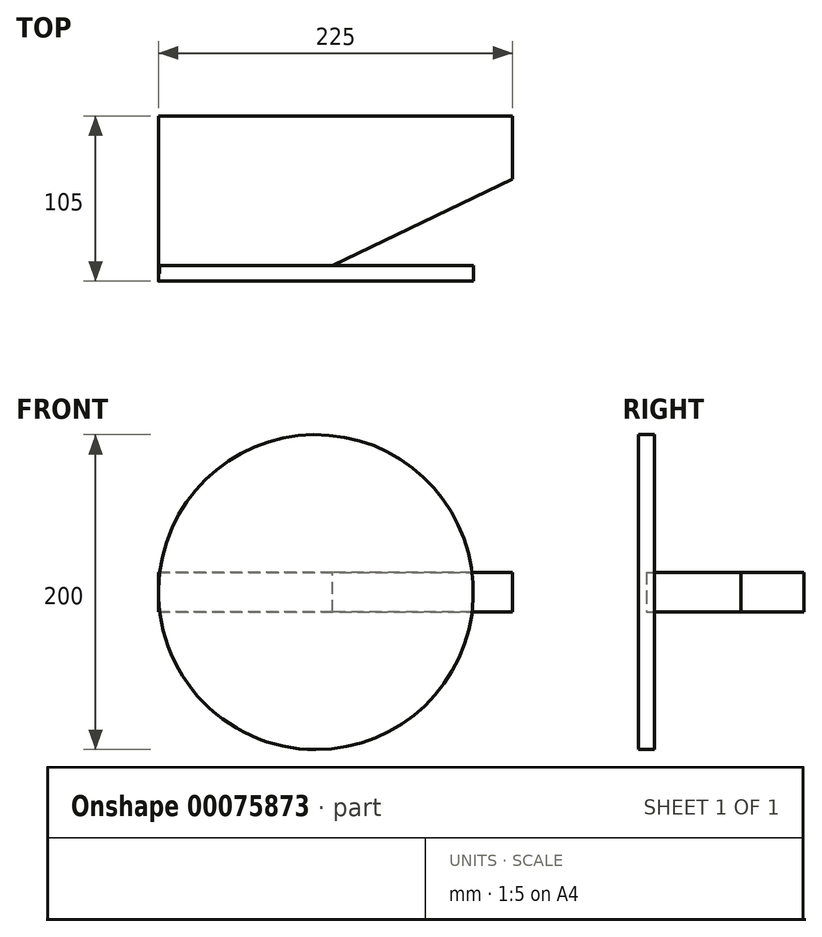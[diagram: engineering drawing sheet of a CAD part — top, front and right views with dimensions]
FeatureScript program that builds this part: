
annotation { "Feature Type Name" : "Feature", "Feature Type Description" : "" }
export const myFeature = defineFeature(function(context is Context, id is Id, definition is map)
    precondition{}
    {
        {
            var Q0;
            Q0=qCreatedBy(makeId("Front.planeOp"),FACE);
            var sketch = newSketch(context, id + "F0", { "sketchPlane" : qUnion([Q0])});
            skCircle(sketch, "E0", {"center": v(0, 0) * mm, "radius": 100 * mm});
            skSolve(sketch);
        }
        {
            var Q0;
            Q0 = qSketchRegion(id + "F0", true);
            extrude(context, id + "F1", {"entities" : qUnion([Q0]), "endBound" : BoundingType.SYMMETRIC, "depth" : 10 * mm});
        }
        {
            var Q0;
            Q0=qCreatedBy(makeId("Top.planeOp"),FACE);
            var sketch = newSketch(context, id + "F2", { "sketchPlane" : qUnion([Q0])});
            skLineSegment(sketch, "E1", {"start": v(0, 0) * mm, "end": v(-100, 0) * mm});
            skLineSegment(sketch, "E2", {"start": v(-100, 0) * mm, "end": v(-100, 100) * mm});
            skLineSegment(sketch, "E3", {"start": v(-100, 100) * mm, "end": v(125, 100) * mm});
            skLineSegment(sketch, "E4", {"start": v(125, 100) * mm, "end": v(125, 60) * mm});
            skLineSegment(sketch, "E5", {"start": v(125, 60) * mm, "end": v(0, 0) * mm});
            skSolve(sketch);
        }
        {
            var Q0;
            Q0 = qSketchRegion(id + "F2", true);
            extrude(context, id + "F3", {"entities" : qUnion([Q0]), "operationType" : NewBodyOperationType.ADD, "endBound" : BoundingType.SYMMETRIC, "depth" : 25 * mm, "offsetDistance" : 25 * mm});
        }
    });
